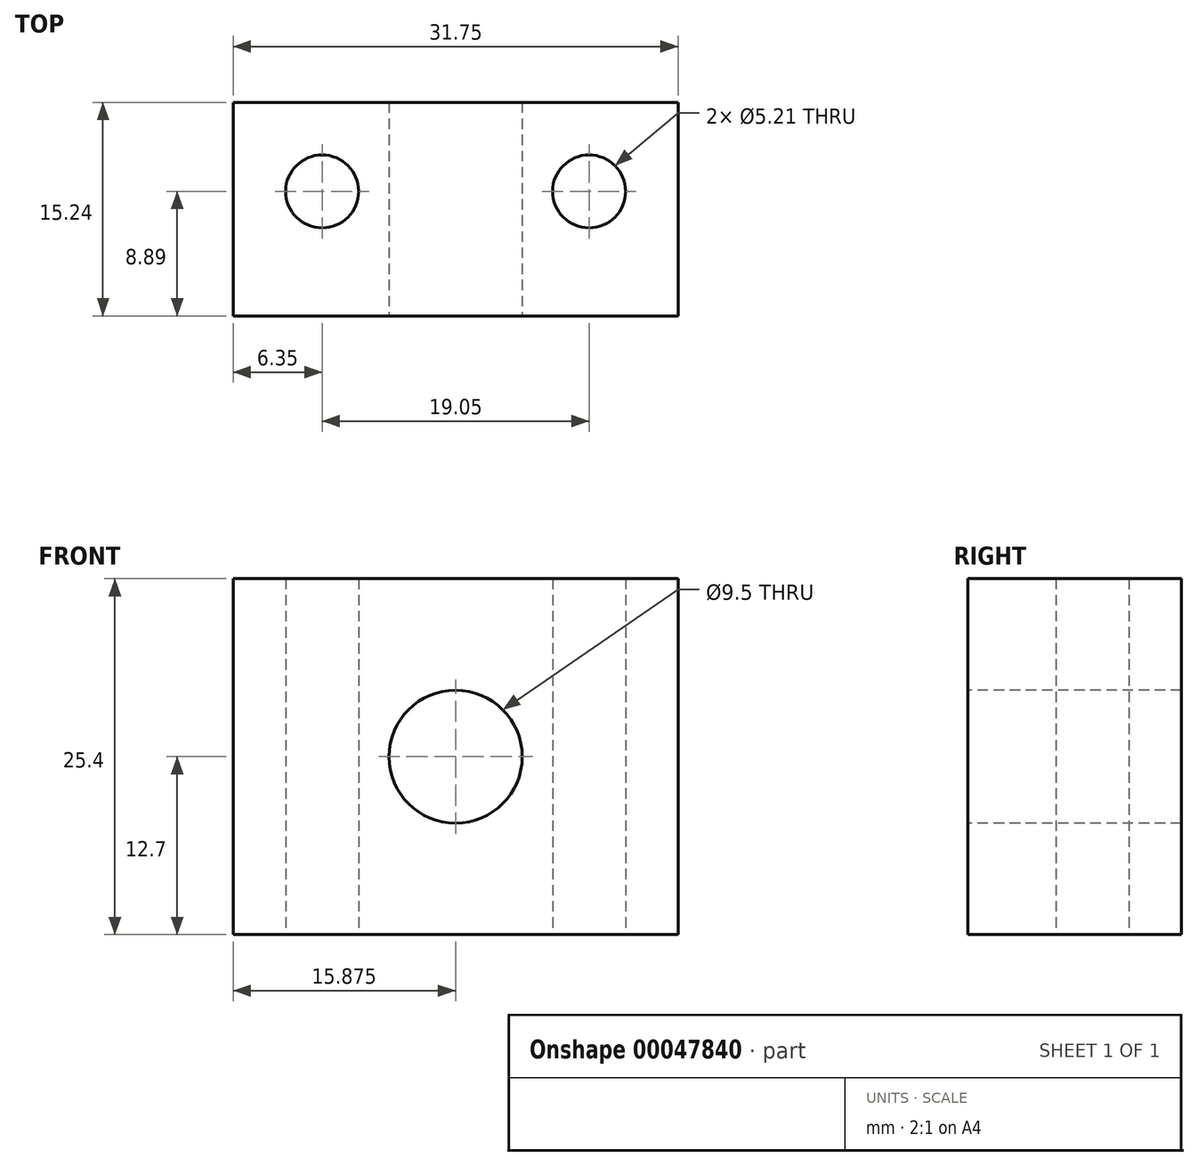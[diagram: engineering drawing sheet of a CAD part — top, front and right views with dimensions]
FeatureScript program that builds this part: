
annotation { "Feature Type Name" : "Feature", "Feature Type Description" : "" }
export const myFeature = defineFeature(function(context is Context, id is Id, definition is map)
    precondition{}
    {
        {
            var Q0;
            Q0=qCreatedBy(makeId("Front.planeOp"),FACE);
            var sketch = newSketch(context, id + "F0", { "sketchPlane" : qUnion([Q0])});
            skLineSegment(sketch, "E0.bottom", {"start": v(0, 0) * mm, "end": v(31.75, 0) * mm});
            skLineSegment(sketch, "E0.top", {"start": v(0, 25.4) * mm, "end": v(31.75, 25.4) * mm});
            skLineSegment(sketch, "E0.left", {"start": v(0, 0) * mm, "end": v(0, 25.4) * mm});
            skLineSegment(sketch, "E0.right", {"start": v(31.75, 0) * mm, "end": v(31.75, 25.4) * mm});
            skSolve(sketch);
        }
        {
            var Q0;
            Q0=makeQuery(id+"F0.imprint","IMPRINT",FACE,{"disambiguationData":[TD([[makeQuery(id+"F0.imprint","IMPRINT",EDGE,{"derivedFrom":sQuery(id+"F0.wireOp",EDGE,"E0.bottom")}),1.0]])]});
            extrude(context, id + "F1", {"entities" : qUnion([Q0]), "depth" : 12.7 * mm});
        }
        {
            var Q0;
            Q0=makeQuery(id+"F1.opExtrude","CAP_FACE",FACE,{"disambiguationData":[OSD([sQuery(id+"F0.wireOp",EDGE,"E0.bottom"),sQuery(id+"F0.wireOp",EDGE,"E0.top"),sQuery(id+"F0.wireOp",EDGE,"E0.left"),sQuery(id+"F0.wireOp",EDGE,"E0.right")])],"isStart":false});
            var sketch = newSketch(context, id + "F2", { "sketchPlane" : qUnion([Q0])});
            skLineSegment(sketch, "E1", {"start": v(0, 12.7) * mm, "end": v(31.75, 12.7) * mm, "construction": true});
            skLineSegment(sketch, "E2", {"start": v(15.87, 25.4) * mm, "end": v(15.87, 0) * mm, "construction": true});
            skLineSegment(sketch, "E3", {"start": v(15.87, 0) * mm, "end": v(16.16, 0.22) * mm, "construction": true});
            skCircle(sketch, "E4", {"center": v(15.87, 12.7) * mm, "radius": 4.75 * mm});
            skSolve(sketch);
        }
        {
            var Q0;
            Q0=makeQuery(id+"F2.imprint","IMPRINT",FACE,{"disambiguationData":[TD([[makeQuery(id+"F2.imprint","IMPRINT",EDGE,{"derivedFrom":sQuery(id+"F2.wireOp",EDGE,"E4")}),1.0]])]});
            extrude(context, id + "F3", {"entities" : qUnion([Q0]), "operationType" : NewBodyOperationType.REMOVE, "endBound" : BoundingType.UP_TO_NEXT, "oppositeDirection" : true, "depth" : 25.4 * mm});
        }
        {
            var Q0;
            Q0=makeQuery(id+"F1.opExtrude","CAP_FACE",FACE,{"disambiguationData":[OSD([sQuery(id+"F0.wireOp",EDGE,"E0.bottom"),sQuery(id+"F0.wireOp",EDGE,"E0.top"),sQuery(id+"F0.wireOp",EDGE,"E0.left"),sQuery(id+"F0.wireOp",EDGE,"E0.right")])],"isStart":false});
            var sketch = newSketch(context, id + "F4", { "sketchPlane" : qUnion([Q0])});
            skCircle(sketch, "E5", {"center": v(15.87, 12.7) * mm, "radius": 9.53 * mm});
            skCircle(sketch, "E6", {"center": v(15.87, 12.7) * mm, "radius": 3.97 * mm});
            skCircle(sketch, "E7.0", {"center": v(15.87, 12.7) * mm, "radius": 4.75 * mm, "construction": true});
            skSolve(sketch);
        }
        {
            var Q0;
            Q0=makeQuery(id+"F4.imprint","IMPRINT",FACE,{"disambiguationData":[TD([[makeQuery(id+"F4.imprint","IMPRINT",EDGE,{"derivedFrom":sQuery(id+"F4.wireOp",EDGE,"E5")}),1.0]])]});
            var Q1;
            Q1=makeQuery(id+"F4.imprint","IMPRINT",FACE,{"disambiguationData":[TD([[makeQuery(id+"F4.imprint","IMPRINT",EDGE,{"derivedFrom":sQuery(id+"F4.wireOp",EDGE,"E6")}),-1.0]])]});
            extrude(context, id + "F5", {"entities" : qUnion([Q0, Q1]), "depth" : 3.17 * mm});
        }
        {
            var Q0;
            Q0=makeQuery(id+"F1.opExtrude","SWEPT_FACE",FACE,{"disambiguationData":[OSD([sQuery(id+"F0.wireOp",EDGE,"E0.bottom")])]});
            var sketch = newSketch(context, id + "F6", { "sketchPlane" : qUnion([Q0])});
            skLineSegment(sketch, "E8", {"start": v(0, 6.35) * mm, "end": v(31.75, 6.35) * mm, "construction": true});
            skPoint(sketch, "E9", {"position": v(6.35, 6.35) * mm});
            skPoint(sketch, "E10", {"position": v(25.4, 6.35) * mm});
            skSolve(sketch);
        }
        {
            var Q0;
            Q0=sQuery(id+"F6.wireOp",VERTEX,"E9");
            var Q1;
            Q1=sQuery(id+"F6.wireOp",VERTEX,"E10");
            var Q2;
            Q2=makeQuery(id+"F1.opExtrude","SWEPT_BODY",BODY,{"disambiguationData":[OSD([sQuery(id+"F0.wireOp",EDGE,"E0.bottom"),sQuery(id+"F0.wireOp",EDGE,"E0.top"),sQuery(id+"F0.wireOp",EDGE,"E0.left"),sQuery(id+"F0.wireOp",EDGE,"E0.right")])]});
            hole(context, id + "F7", {"style" : HoleStyle.SIMPLE, "holeDiameter" : 5.2 * mm, "endStyle" : HoleEndStyle.THROUGH, "locations" : qUnion([Q0, Q1]), "scope" : qUnion([Q2])});
        }
        {
            var Q0;
            Q0=makeQuery(id+"F5.opExtrude","SWEPT_BODY",BODY,{"disambiguationData":[OSD([sQuery(id+"F4.wireOp",EDGE,"E5"),sQuery(id+"F4.wireOp",EDGE,"E6")])]});
            deleteBodies(context, id + "F8", {"entities" : qUnion([Q0])});
        }
        {
            var Q0;
            Q0=makeQuery(id+"F4.imprint","IMPRINT",FACE,{"disambiguationData":[TD([[makeQuery(id+"F4.imprint","IMPRINT",EDGE,{"derivedFrom":sQuery(id+"F4.wireOp",EDGE,"E5")}),-1.0]])]});
            var Q1;
            Q1=makeQuery(id+"F4.imprint","IMPRINT",FACE,{"disambiguationData":[TD([[makeQuery(id+"F4.imprint","IMPRINT",EDGE,{"derivedFrom":sQuery(id+"F4.wireOp",EDGE,"E5")}),1.0]])]});
            extrude(context, id + "F9", {"entities" : qUnion([Q0, Q1]), "operationType" : NewBodyOperationType.ADD, "depth" : 2.54 * mm});
        }
    });
